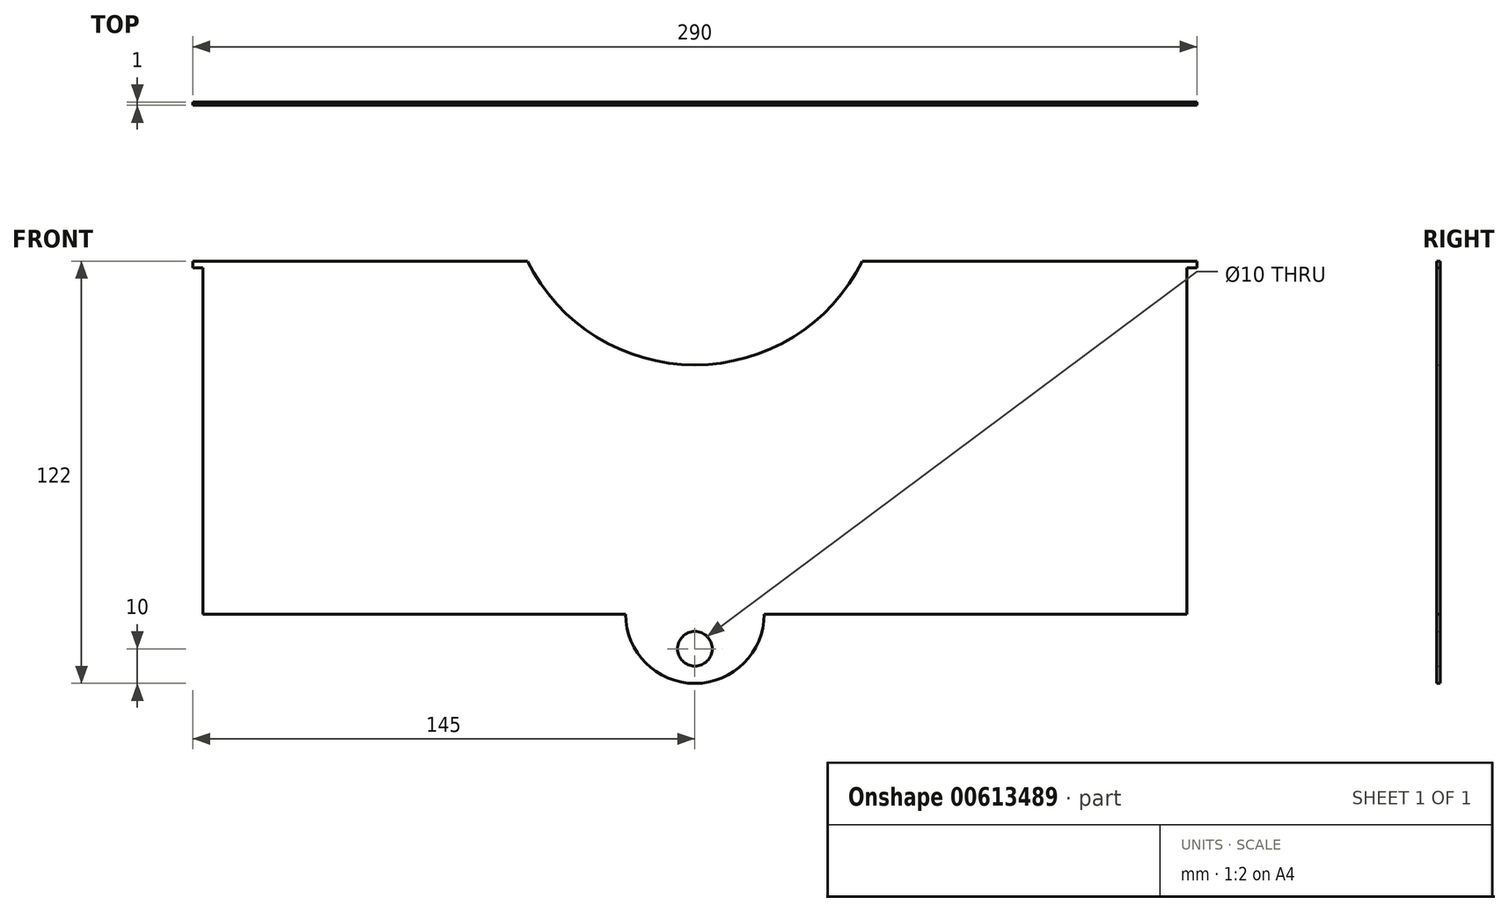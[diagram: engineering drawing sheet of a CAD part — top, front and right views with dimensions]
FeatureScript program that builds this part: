
annotation { "Feature Type Name" : "Feature", "Feature Type Description" : "" }
export const myFeature = defineFeature(function(context is Context, id is Id, definition is map)
    precondition{}
    {
        {
            var Q0;
            Q0=qCreatedBy(makeId("Front.planeOp"),FACE);
            var sketch = newSketch(context, id + "F0", { "sketchPlane" : qUnion([Q0])});
            skLineSegment(sketch, "E0", {"start": v(-145, 102) * mm, "end": v(-145, 100) * mm});
            skLineSegment(sketch, "E1", {"start": v(-145, 100) * mm, "end": v(-142, 100) * mm});
            skLineSegment(sketch, "E2", {"start": v(-142, 100) * mm, "end": v(-142, 0) * mm});
            skLineSegment(sketch, "E3", {"start": v(-142, 0) * mm, "end": v(-20, 0) * mm});
            skLineSegment(sketch, "E4", {"start": v(142, 0) * mm, "end": v(20, 0) * mm});
            skLineSegment(sketch, "E5", {"start": v(142, 0) * mm, "end": v(142, 100) * mm});
            skLineSegment(sketch, "E6", {"start": v(142, 100) * mm, "end": v(145, 100) * mm});
            skLineSegment(sketch, "E7", {"start": v(145, 100) * mm, "end": v(145, 102) * mm});
            skLineSegment(sketch, "E8", {"start": v(145, 102) * mm, "end": v(-145, 102) * mm});
            skArc(sketch, "E9", {"start": v(-20, 0) * mm, "mid": v(0, -20) * mm, "end": v(20, 0) * mm});
            skCircle(sketch, "E10", {"center": v(0, -10) * mm, "radius": 5 * mm});
            skSolve(sketch);
        }
        {
            var Q0;
            Q0 = qSketchRegion(id + "F0", true);
            extrude(context, id + "F1", {"entities" : qUnion([Q0]), "depth" : 1 * mm, "offsetDistance" : 25 * mm});
        }
        {
            var Q0;
            Q0=qCreatedBy(makeId("Front.planeOp"),FACE);
            var sketch = newSketch(context, id + "F2", { "sketchPlane" : qUnion([Q0])});
            skLineSegment(sketch, "E11", {"start": v(-222.74, 51) * mm, "end": v(218.86, 51) * mm, "construction": true});
            skLineSegment(sketch, "E12", {"start": v(-226.34, 126) * mm, "end": v(220.06, 126) * mm, "construction": true});
            skCircle(sketch, "E13", {"center": v(0, 126) * mm, "radius": 54 * mm});
            skPoint(sketch, "E13.centerSnap0", {"position": v(-3.14, 126) * mm});
            skSolve(sketch);
        }
        {
            var Q0;
            Q0 = qSketchRegion(id + "F2", true);
            extrude(context, id + "F3", {"entities" : qUnion([Q0]), "operationType" : NewBodyOperationType.REMOVE, "depth" : 1 * mm, "offsetDistance" : 25 * mm});
        }
    });
